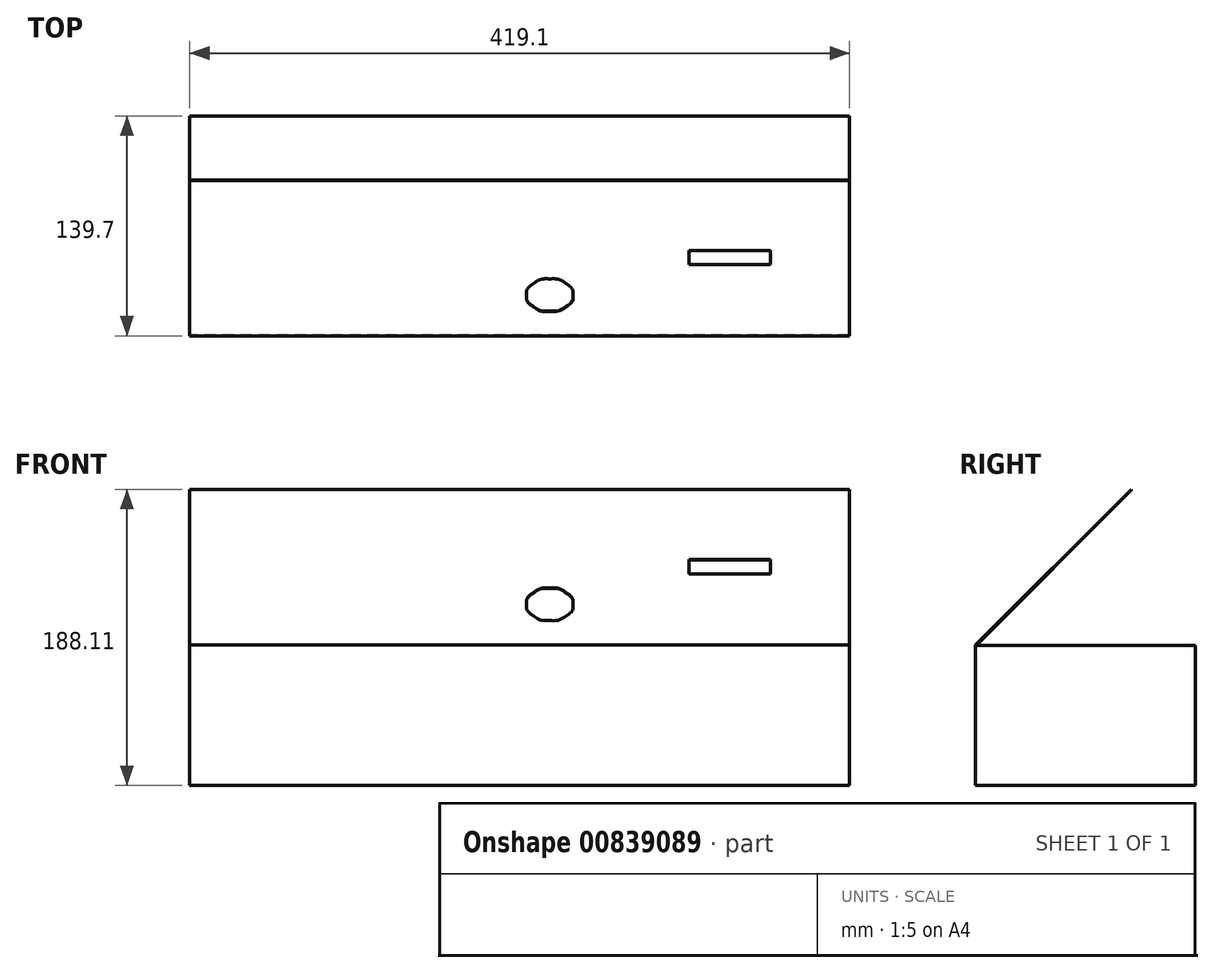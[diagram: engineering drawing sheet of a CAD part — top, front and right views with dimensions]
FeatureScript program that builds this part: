
annotation { "Feature Type Name" : "Feature", "Feature Type Description" : "" }
export const myFeature = defineFeature(function(context is Context, id is Id, definition is map)
    precondition{}
    {
        {
            var Q0;
            Q0=qCreatedBy(makeId("Right.planeOp"),FACE);
            var sketch = newSketch(context, id + "F0", { "sketchPlane" : qUnion([Q0])});
            skLineSegment(sketch, "E0.bottom", {"start": v(0, 0) * mm, "end": v(-139.7, 0) * mm});
            skLineSegment(sketch, "E0.top", {"start": v(0, 88.9) * mm, "end": v(-139.3, 88.9) * mm});
            skLineSegment(sketch, "E0.left", {"start": v(0, 0) * mm, "end": v(0, 88.9) * mm});
            skLineSegment(sketch, "E0.right", {"start": v(-139.7, 0) * mm, "end": v(-139.7, 89.32) * mm});
            skLineSegment(sketch, "E1", {"start": v(-139.7, 89.32) * mm, "end": v(-40.92, 188.1) * mm});
            skLineSegment(sketch, "E2", {"start": v(-40.92, 188.1) * mm, "end": v(-40.63, 187.82) * mm});
            skLineSegment(sketch, "E3", {"start": v(-40.63, 187.82) * mm, "end": v(-139.3, 89.15) * mm});
            skLineSegment(sketch, "E4", {"start": v(-139.3, 88.9) * mm, "end": v(-139.3, 89.15) * mm});
            skLineSegment(sketch, "E5", {"start": v(-139.3, 88.9) * mm, "end": v(-139.7, 88.9) * mm, "construction": true});
            skSolve(sketch);
        }
        {
            var Q0;
            Q0=qSketchRegion(id+"F0",true);
            extrude(context, id + "F1", {"entities" : qUnion([Q0]), "endBound" : BoundingType.SYMMETRIC, "depth" : 419.1 * mm, "offsetDistance" : 25.4 * mm});
        }
        {
            var Q0;
            Q0=makeQuery(id+"F1.opExtrude","SWEPT_FACE",FACE,{"disambiguationData":[OSD([sQuery(id+"F0.wireOp",EDGE,"E1")])]});
            var sketch = newSketch(context, id + "F2", { "sketchPlane" : qUnion([Q0])});
            skLineSegment(sketch, "E6", {"start": v(-209.55, -35.2) * mm, "end": v(-209.55, 103.7) * mm, "construction": true});
            skLineSegment(sketch, "E7", {"start": v(107.55, 28.3) * mm, "end": v(159.14, 28.3) * mm});
            skLineSegment(sketch, "E8", {"start": v(209.55, -35.2) * mm, "end": v(209.55, 103.7) * mm, "construction": true});
            skLineSegment(sketch, "E9", {"start": v(159.14, 28.3) * mm, "end": v(159.14, 41) * mm});
            skLineSegment(sketch, "E10", {"start": v(159.14, 41) * mm, "end": v(107.55, 41) * mm});
            skLineSegment(sketch, "E11", {"start": v(107.55, 41) * mm, "end": v(107.55, 28.3) * mm});
            skLineSegment(sketch, "E12", {"start": v(-209.55, 103.7) * mm, "end": v(209.55, 103.7) * mm, "construction": true});
            skLineSegment(sketch, "E13", {"start": v(209.55, -35.2) * mm, "end": v(-209.55, -35.2) * mm, "construction": true});
            skFitSpline(sketch, "E14", {"points": [v(19.05, 15.6) * mm, v(15.2, 15.6) * mm, v(11.38, 14.01) * mm, v(8.66, 11.3) * mm]});
            skFitSpline(sketch, "E15", {"points": [v(8.66, 11.3) * mm, v(5.95, 8.57) * mm, v(4.36, 4.75) * mm, v(4.36, 0.9) * mm, v(4.36, -2.93) * mm, v(5.95, -6.76) * mm, v(8.66, -9.47) * mm]});
            skFitSpline(sketch, "E16", {"points": [v(8.66, -9.47) * mm, v(11.38, -12.2) * mm, v(15.2, -13.77) * mm, v(19.05, -13.77) * mm, v(22.9, -13.77) * mm, v(26.71, -12.2) * mm, v(29.43, -9.47) * mm, v(32.15, -6.76) * mm, v(33.73, -2.93) * mm, v(33.73, 0.9) * mm, v(33.73, 4.75) * mm, v(32.15, 8.57) * mm, v(29.43, 11.3) * mm]});
            skFitSpline(sketch, "E17", {"points": [v(29.43, 11.3) * mm, v(26.71, 14.01) * mm, v(22.9, 15.6) * mm, v(19.05, 15.6) * mm]});
            skSolve(sketch);
        }
        {
            var Q0;
            Q0=qSketchRegion(id+"F2",true);
            var Q1;
            Q1=makeQuery(id+"F1.opExtrude","SWEPT_FACE",FACE,{"disambiguationData":[OSD([sQuery(id+"F0.wireOp",EDGE,"E3")])]});
            extrude(context, id + "F3", {"entities" : qUnion([Q0]), "operationType" : NewBodyOperationType.REMOVE, "endBound" : BoundingType.UP_TO_SURFACE, "oppositeDirection" : true, "depth" : 25.4 * mm, "endBoundEntityFace" : qUnion([Q1]), "offsetDistance" : 25.4 * mm});
        }
    });
